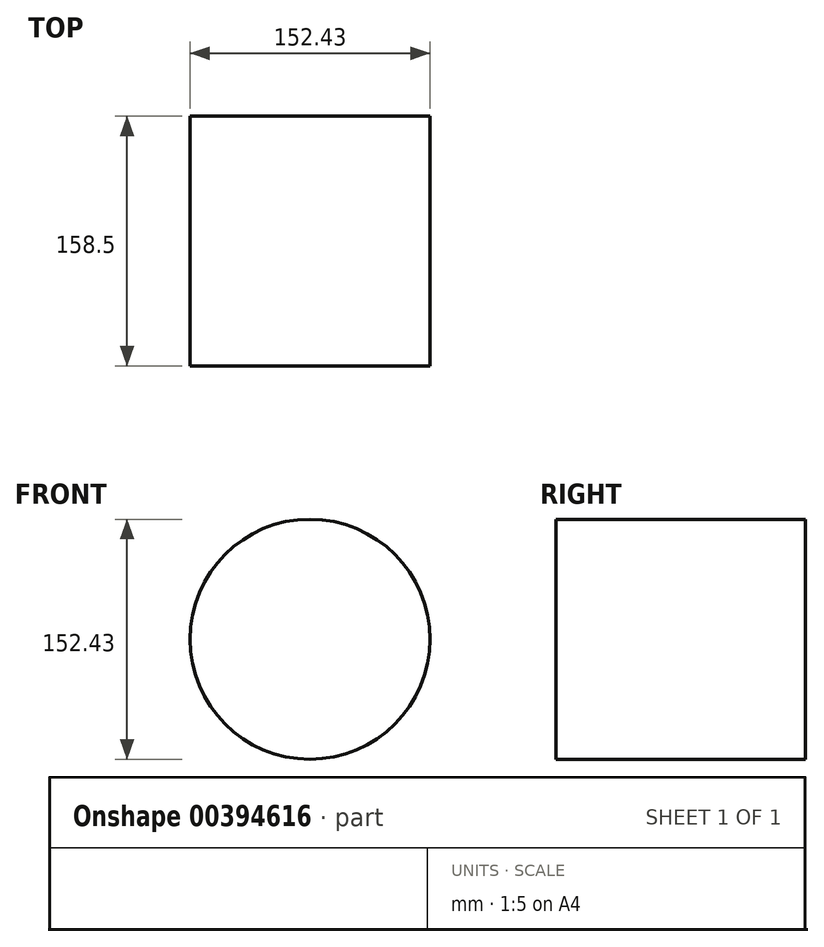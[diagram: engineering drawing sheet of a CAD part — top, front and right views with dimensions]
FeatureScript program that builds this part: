
annotation { "Feature Type Name" : "Feature", "Feature Type Description" : "" }
export const myFeature = defineFeature(function(context is Context, id is Id, definition is map)
    precondition{}
    {
        {
            var Q0;
            Q0=qCreatedBy(makeId("Front.planeOp"),FACE);
            var sketch = newSketch(context, id + "F0", { "sketchPlane" : qUnion([Q0])});
            skCircle(sketch, "E0", {"center": v(-2.09, -2.84) * mm, "radius": 76.22 * mm});
            skSolve(sketch);
        }
        {
            var Q0;
            Q0=makeQuery(id+"F0.imprint","IMPRINT",FACE,{"disambiguationData":[TD([[makeQuery(id+"F0.imprint","IMPRINT",EDGE,{"derivedFrom":sQuery(id+"F0.wireOp",EDGE,"E0")}),1.0]])]});
            extrude(context, id + "F1", {"entities" : qUnion([Q0]), "depth" : 158.5 * mm});
        }
    });
